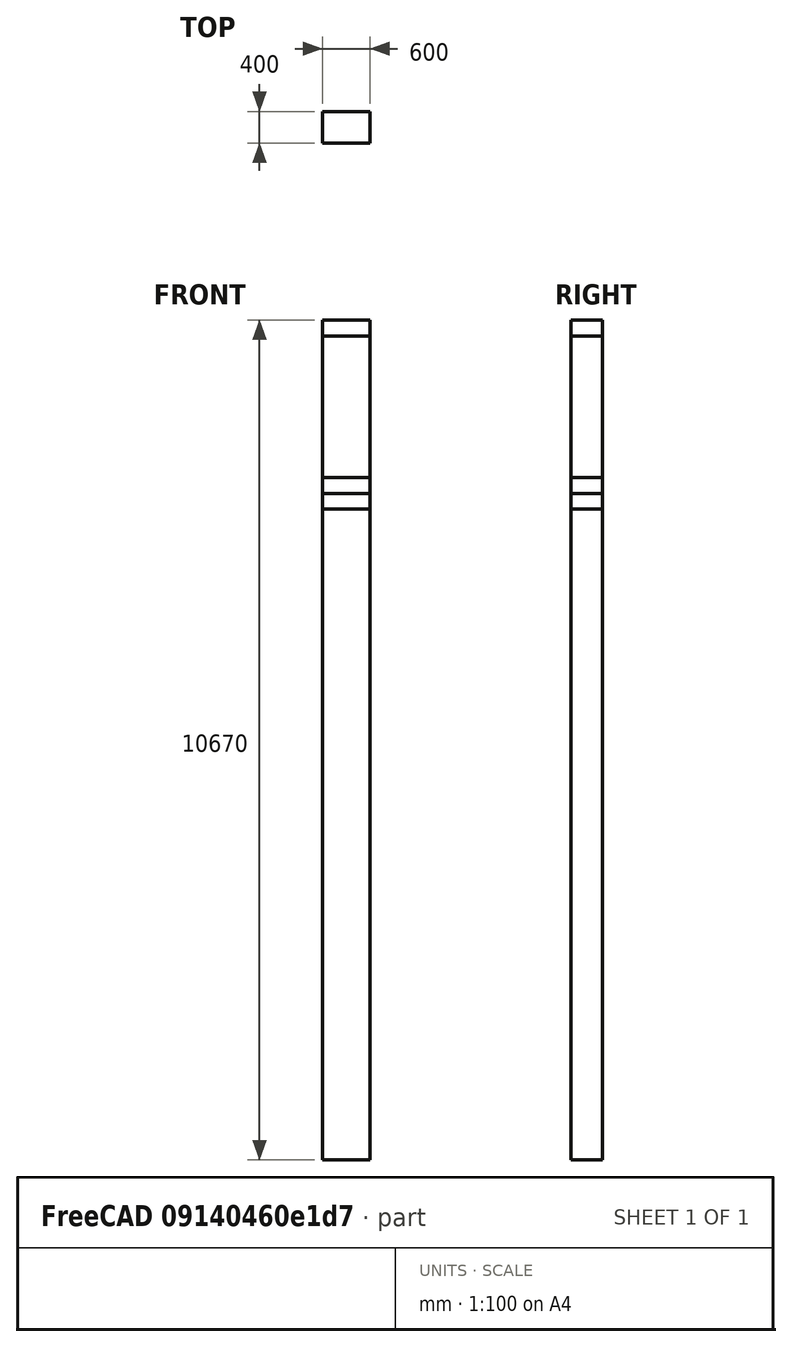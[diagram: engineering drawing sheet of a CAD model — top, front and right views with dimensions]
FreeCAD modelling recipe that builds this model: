
FCSTD DOCUMENT  (FreeCAD 0.21R33694 (Git))
Label: column_3
License: All rights reserved
LicenseURL: http://en.wikipedia.org/wiki/All_rights_reserved
objects: Fem::ConstraintForce×10, Part::FeaturePython×7, Part::Feature×5, Part::Plane×4, Fem::ConstraintFixed×2, Fem::FemSolverObjectPython×1, App::MaterialObjectPython×1, Part::Box×1, Fem::FemMeshObjectPython×1, Fem::FemAnalysis×1
note: 17 computed .brp shape members not serialized (recipe doc carries the construction recipe); baked Part::Feature solids carry a one-line shape summary decoded from their .brp

FEATURE [Fem::FemSolverObjectPython] SolverCcxTools  # FEM object (typed FeaturePython)
  AnalysisType = 0
  BeamShellResultOutput3D = true
  BucklingFactors = 1
  EigenmodeHighLimit = 1000000
  EigenmodeLowLimit = 0
  EigenmodesCount = 10
  GeometricalNonlinearity = 0
  IterationsControlParameterCutb = 0.25,0.5,0.75,0.85,,,1.5,
  IterationsControlParameterIter = 4,8,9,200,10,400,,200,,
  IterationsControlParameterTimeUse = false
  IterationsThermoMechMaximum = 2000
  IterationsUserDefinedIncrementations = false
  IterationsUserDefinedTimeStepLength = false
  MaterialNonlinearity = 0
  MatrixSolverType = 0
  SplitInputWriter = true
  ThermoMechSteadyState = true
  TimeEnd = 1
  TimeInitialStep = 0.01
FEATURE [App::MaterialObjectPython] MaterialSolid  label="B450"  # material (typed FeaturePython)
  Category = 0
  Material = AngleOfFriction=30 deg,AuthorAndLicense=(c) 2019 Bernd Hahnebach (CC-BY 3.0),CardName=Concrete-EN-C35_45,CompressiveStrength=15.75 MPa,+7 more (map truncated)
FEATURE [Fem::ConstraintFixed] ConstraintFixed
  NormalDirection = (0,0,-1)
FEATURE [Part::Box] Box  label="Cube"
  AttacherType = Attacher::AttachEngine3D
  Height = 10670
  Length = 600
  Width = 400
FEATURE [Part::Plane] Plane
  AttacherType = Attacher::AttachEngine3D
  Length = 600
  Placement = pos=(0,0,8270) rot=(0,0,1;0rad)
  Width = 400
FEATURE [Part::Plane] Plane002
  AttacherType = Attacher::AttachEngine3D
  Length = 600
  Placement = pos=(0,0,8470) rot=(0,0,1;0rad)
  Width = 400
FEATURE [Part::Plane] Plane003
  AttacherType = Attacher::AttachEngine3D
  Length = 600
  Placement = pos=(0,0,8670) rot=(0,0,1;0rad)
  Width = 400
FEATURE [Part::Plane] Plane004
  AttacherType = Attacher::AttachEngine3D
  Length = 600
  Placement = pos=(0,0,10470) rot=(0,0,1;0rad)
  Width = 400
FEATURE [Part::FeaturePython] Slice  # WARN: FeaturePython — macro-defined, semantics opaque (R4)
  Base = -> Box
  Mode = 1
  Tolerance = 0
  Tools = -> [Plane,Plane002,Plane003,Plane004]
FEATURE [Part::FeaturePython] Slice_child0  label="Slice.0"  # WARN: FeaturePython — macro-defined, semantics opaque (R4)
  Base = -> Slice
  FilterType = 1
  Invert = false
  OverrideMaxVal = 0
  WindowFrom = 80
  WindowTo = 100
  items = 0
FEATURE [Part::FeaturePython] Slice_child1  label="Slice.1"  # WARN: FeaturePython — macro-defined, semantics opaque (R4)
  Base = -> Slice
  FilterType = 1
  Invert = false
  OverrideMaxVal = 0
  WindowFrom = 80
  WindowTo = 100
  items = 1
FEATURE [Fem::ConstraintForce] ConstraintForce004  label="crane_z2(p)"
  Direction = -> Slice_child1 [Edge3]
  DirectionVector = (0,0,1)
  Force = 250000
  NormalDirection = (-1,0,0)
  Points = (16) [(0,400,8270),(0,400,8336.67),(0,400,8403.33),(0,400,8470),(0,266.667,8270),(0,266.667,8336.67),(0,266.667,8403.33),(0,266.667,8470),(0,133.333,8270),+7 more]
  References = -> [Slice_child1]
  Scale = 19
FEATURE [Part::FeaturePython] Slice_child2  label="Slice.2"  # WARN: FeaturePython — macro-defined, semantics opaque (R4)
  Base = -> Slice
  FilterType = 1
  Invert = false
  OverrideMaxVal = 0
  WindowFrom = 80
  WindowTo = 100
  items = 2
FEATURE [Fem::ConstraintForce] ConstraintForce003  label="crane_z1(p)"
  Direction = -> Slice_child2 [Edge5]
  DirectionVector = (0,0,-1)
  Force = 550000
  NormalDirection = (1,0,0)
  Points = (16) [(600,400,8270),(600,400,8336.67),(600,400,8403.33),(600,400,8470),(600,266.667,8270),(600,266.667,8336.67),(600,266.667,8403.33),(600,266.667,8470),+8 more]
  References = -> [Slice_child1]
  Reversed = true
  Scale = 19
FEATURE [Fem::ConstraintForce] ConstraintForce005  label="mast_x2"
  DirectionVector = (-1,0,0)
  Force = 9430
  NormalDirection = (-1,0,0)
  Points = (16) [(0,400,8470),(0,400,8536.67),(0,400,8603.33),(0,400,8670),(0,266.667,8470),(0,266.667,8536.67),(0,266.667,8603.33),(0,266.667,8670),(0,133.333,8470),+7 more]
  References = -> [Slice_child2]
  Scale = 19
FEATURE [Part::FeaturePython] Slice_child3  label="Slice.3"  # WARN: FeaturePython — macro-defined, semantics opaque (R4)
  Base = -> Slice
  FilterType = 1
  Invert = false
  OverrideMaxVal = 0
  WindowFrom = 80
  WindowTo = 100
  items = 3
FEATURE [Part::FeaturePython] Slice_child4  label="Slice.4"  # WARN: FeaturePython — macro-defined, semantics opaque (R4)
  Base = -> Slice
  FilterType = 1
  Invert = false
  OverrideMaxVal = 0
  WindowFrom = 80
  WindowTo = 100
  items = 4
FEATURE [Fem::ConstraintForce] ConstraintForce  label="wind"
  DirectionVector = (1,0,0)
  Force = 42000
  NormalDirection = (-1,0,0)
  Points = (132) [(0,400,10470),(0,400,10536.7),(0,400,10603.3),(0,400,10670),(0,266.667,10470),(0,266.667,10536.7),(0,266.667,10603.3),(0,266.667,10670),+124 more]
  References = -> [Slice_child4,Slice_child3,Slice_child2,Slice_child1,Slice_child0]
  Reversed = true
  Scale = 59
FEATURE [Fem::ConstraintForce] ConstraintForce001  label="mast_x1"
  DirectionVector = (1,0,0)
  Force = 12820
  NormalDirection = (-1,0,0)
  Points = (16) [(0,400,10470),(0,400,10536.7),(0,400,10603.3),(0,400,10670),(0,266.667,10470),(0,266.667,10536.7),(0,266.667,10603.3),(0,266.667,10670),+8 more]
  References = -> [Slice_child4]
  Reversed = true
  Scale = 19
FEATURE [Fem::ConstraintForce] ConstraintForce002  label="beam(p)"
  DirectionVector = (0,0,-1)
  Force = 100000
  NormalDirection = (0,0,1)
  Points = (16) [(0,0,10670),(200,0,10670),(400,0,10670),(600,0,10670),(0,133.333,10670),(200,133.333,10670),(400,133.333,10670),(600,133.333,10670),(0,266.667,10670),+7 more]
  References = -> [Slice_child4]
  Reversed = true
  Scale = 24
FEATURE [Part::Feature] Solid
  shape: bbox 600 x 400 x 8270 mm, 6 faces (baked)
FEATURE [Part::Feature] Solid001
  shape: bbox 600 x 400 x 200 mm, 6 faces (baked)
FEATURE [Part::Feature] Solid002
  shape: bbox 600 x 400 x 200 mm, 6 faces (baked)
FEATURE [Part::Feature] Solid003
  shape: bbox 600 x 400 x 1800 mm, 6 faces (baked)
FEATURE [Part::Feature] Solid004
  shape: bbox 600 x 400 x 200 mm, 6 faces (baked)
FEATURE [Part::FeaturePython] BooleanFragments  # WARN: FeaturePython — macro-defined, semantics opaque (R4)
  Mode = 2
  Objects = -> [Solid,Solid001,Solid002,Solid003,Solid004]
  Tolerance = 0
FEATURE [Fem::FemMeshObjectPython] FEMMeshGmsh  # FEM object (typed FeaturePython)
  Algorithm2D = 0
  Algorithm3D = 0
  CharacteristicLengthMax = 400
  CharacteristicLengthMin = 0
  CoherenceMesh = true
  ElementDimension = 0
  ElementOrder = 1
  GeometryTolerance = 1e-06
  GroupsOfNodes = false
  HighOrderOptimize = 0
  MeshSizeFromCurvature = 12
  OptimizeNetgen = false
  OptimizeStd = true
  Part = -> BooleanFragments
  RecombinationAlgorithm = 0
  Recombine3DAll = false
  RecombineAll = false
  SecondOrderLinear = false
FEATURE [Fem::ConstraintFixed] ConstraintFixed001  label="foundation"
  NormalDirection = (0,0,-1)
  Normals = (16) [(0,0,-1),(0,0,-1),(0,0,-1),(0,0,-1),(0,0,-1),(0,0,-1),(0,0,-1),(0,0,-1),(0,0,-1),(0,0,-1),(0,0,-1),(0,0,-1),(0,0,-1),(0,0,-1),(0,0,-1),(0,0,-1)]
  Points = (16) [(0,0,0),(200,0,0),(400,0,0),(600,0,0),(0,133.333,0),(200,133.333,0),(400,133.333,0),(600,133.333,0),(0,266.667,0),(200,266.667,0),(400,266.667,0),+5 more]
  References = -> [Slice_child0]
  Scale = 24
FEATURE [Fem::ConstraintForce] ConstraintForce006  label="mast_y1"
  Direction = -> Slice_child4 [Edge2]
  DirectionVector = (0,1,0)
  Force = 17093
  NormalDirection = (-1,0,0)
  Points = (16) [(0,400,10470),(0,400,10536.7),(0,400,10603.3),(0,400,10670),(0,266.667,10470),(0,266.667,10536.7),(0,266.667,10603.3),(0,266.667,10670),+8 more]
  References = -> [Slice_child4]
  Scale = 19
FEATURE [Fem::ConstraintForce] ConstraintForce007  label="mast_y2"
  Direction = -> Slice_child4 [Edge9]
  DirectionVector = (0,-1,0)
  Force = 4273
  NormalDirection = (1,0,0)
  Points = (16) [(600,400,10470),(600,400,10536.7),(600,400,10603.3),(600,400,10670),(600,266.667,10470),(600,266.667,10536.7),(600,266.667,10603.3),+9 more]
  References = -> [BooleanFragments]
  Reversed = true
  Scale = 19
FEATURE [Fem::ConstraintForce] ConstraintForce008  label="mast_y3"
  Direction = -> Slice_child2 [Edge2]
  DirectionVector = (0,-1,0)
  Force = 12573
  NormalDirection = (-1,0,0)
  Points = (16) [(0,400,8470),(0,400,8536.67),(0,400,8603.33),(0,400,8670),(0,266.667,8470),(0,266.667,8536.67),(0,266.667,8603.33),(0,266.667,8670),(0,133.333,8470),+7 more]
  References = -> [Slice_child2]
  Reversed = true
  Scale = 19
FEATURE [Fem::ConstraintForce] ConstraintForce009  label="mast_y4"
  Direction = -> Slice_child2 [Edge8]
  DirectionVector = (0,1,0)
  Force = 3143
  NormalDirection = (1,0,0)
  Points = (16) [(600,400,8470),(600,400,8536.67),(600,400,8603.33),(600,400,8670),(600,266.667,8470),(600,266.667,8536.67),(600,266.667,8603.33),(600,266.667,8670),+8 more]
  References = -> [Slice_child2]
  Scale = 19
FEATURE [Fem::FemAnalysis] Analysis
  Group = -> [SolverCcxTools,MaterialSolid,ConstraintForce,ConstraintForce001,ConstraintForce002,ConstraintFixed,ConstraintForce003,ConstraintForce004,ConstraintForce005,FEMMeshGmsh,ConstraintFixed001,ConstraintForce006,ConstraintForce007,ConstraintForce008,ConstraintForce009]
